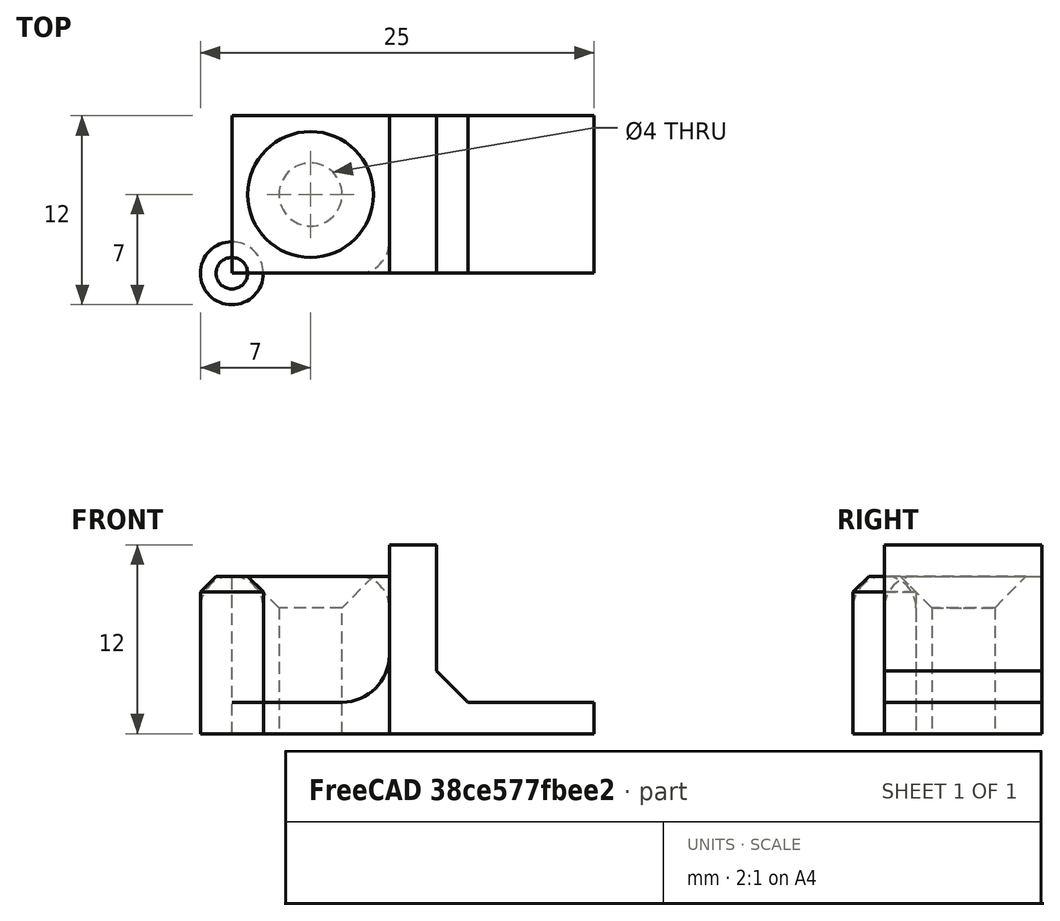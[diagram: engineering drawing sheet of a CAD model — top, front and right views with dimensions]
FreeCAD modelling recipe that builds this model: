
FCSTD DOCUMENT  (FreeCAD 0.18.4R)
Label: Video12
License: All rights reserved
LicenseURL: http://en.wikipedia.org/wiki/All_rights_reserved
objects: Part::Box×6, Part::Chamfer×4, Part::Fillet×3, Part::Cylinder×3, Part::Cut×2, Part::Fuse×1
note: 19 computed .brp shape members not serialized (recipe doc carries the construction recipe); baked Part::Feature solids carry a one-line shape summary decoded from their .brp

FEATURE [Part::Box] Box  label="Cubo"
  AttacherType = Attacher::AttachEngine3D
  Height = 10
  Length = 10
  Width = 10
FEATURE [Part::Fillet] Fillet
  Base = -> Box
  Edges = 3 edges r=2: [Edge5,Edge6,Edge10]
FEATURE [Part::Box] Box001  label="Cubo001"
  AttacherType = Attacher::AttachEngine3D
  Height = 10
  Length = 10
  Width = 10
FEATURE [Part::Chamfer] Chamfer
  Base = -> Box001
  Edges = 3 edges r=2: [Edge5,Edge6,Edge10]
FEATURE [Part::Box] Box002  label="Cubo002"
  AttacherType = Attacher::AttachEngine3D
  Height = 10
  Length = 10
  Width = 10
FEATURE [Part::Cylinder] Cylinder  label="Cilindro"
  Angle = 360
  AttacherType = Attacher::AttachEngine3D
  Height = 10
  Placement = pos=(5,5,0) rot=(0,0,1;0rad)
  Radius = 2
FEATURE [Part::Cut] Cut
  Base = -> Box002
  Tool = -> Cylinder
FEATURE [Part::Chamfer] Chamfer001
  Base = -> Cut
  Edges = 1 edges r=2: [Edge10]
FEATURE [Part::Cylinder] Cylinder001  label="Cilindro001"
  Angle = 360
  AttacherType = Attacher::AttachEngine3D
  Height = 10
  Radius = 2
FEATURE [Part::Fillet] Fillet001
  Base = -> Cylinder001
  Edges = 1 edges r=2: [Edge3]
FEATURE [Part::Cylinder] Cylinder002  label="Cilindro002"
  Angle = 360
  AttacherType = Attacher::AttachEngine3D
  Height = 10
  Radius = 2
FEATURE [Part::Chamfer] Chamfer002
  Base = -> Cylinder002
  Edges = 1 edges r=1: [Edge3]
FEATURE [Part::Box] Box003  label="Cubo003"
  AttacherType = Attacher::AttachEngine3D
  Height = 12
  Length = 23
  Width = 10
FEATURE [Part::Box] Box004  label="Cubo004"
  AttacherType = Attacher::AttachEngine3D
  Height = 10
  Length = 10
  Placement = pos=(0,0,2) rot=(0,0,1;0rad)
  Width = 10
FEATURE [Part::Box] Box005  label="Cubo005"
  AttacherType = Attacher::AttachEngine3D
  Height = 10
  Length = 10
  Placement = pos=(13,0,2) rot=(0,0,1;0rad)
  Width = 10
FEATURE [Part::Fuse] Fusion
  Base = -> Box004
  Tool = -> Box005
FEATURE [Part::Cut] Cut001
  Base = -> Box003
  Tool = -> Fusion
FEATURE [Part::Chamfer] Chamfer003
  Base = -> Cut001
  Edges = 1 edges r=2: [Edge22]
FEATURE [Part::Fillet] Fillet002
  Base = -> Chamfer003
  Edges = 1 edges r=3: [Edge26]
